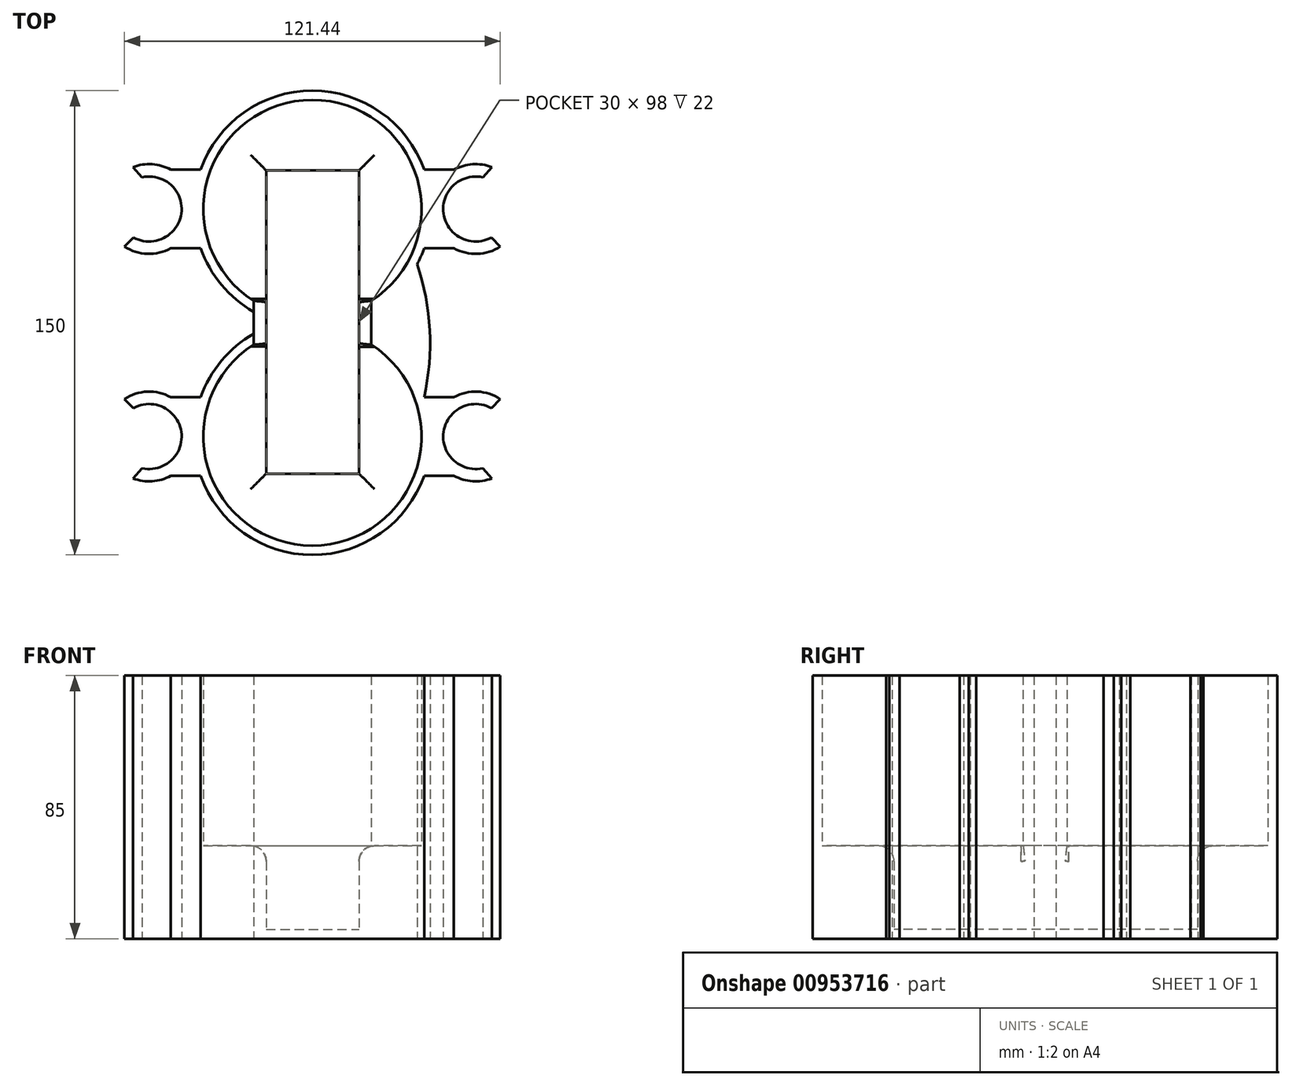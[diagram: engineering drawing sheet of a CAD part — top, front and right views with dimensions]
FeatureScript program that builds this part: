
annotation { "Feature Type Name" : "Feature", "Feature Type Description" : "" }
export const myFeature = defineFeature(function(context is Context, id is Id, definition is map)
    precondition{}
    {
        {
            var Q0;
            Q0=qCreatedBy(makeId("Top.planeOp"),FACE);
            var sketch = newSketch(context, id + "F0", { "sketchPlane" : qUnion([Q0])});
            skCircle(sketch, "E0", {"center": v(0, 36.75) * mm, "radius": 35.25 * mm});
            skCircle(sketch, "E1.0", {"center": v(0, 36.75) * mm, "radius": 38.25 * mm});
            skCircle(sketch, "E2", {"center": v(0, -36.75) * mm, "radius": 35.25 * mm});
            skCircle(sketch, "E3.0", {"center": v(0, -36.75) * mm, "radius": 38.25 * mm});
            skLineSegment(sketch, "E4.bottom", {"start": v(-14.94, 49.23) * mm, "end": v(15.06, 49.23) * mm});
            skLineSegment(sketch, "E4.top", {"start": v(-14.94, -48.77) * mm, "end": v(15.06, -48.77) * mm});
            skLineSegment(sketch, "E4.left", {"start": v(-14.94, 49.23) * mm, "end": v(-14.94, -48.77) * mm});
            skLineSegment(sketch, "E4.right", {"start": v(15.06, 49.23) * mm, "end": v(15.06, -48.77) * mm});
            skLineSegment(sketch, "E5", {"start": v(19, 7.06) * mm, "end": v(19, -7.06) * mm});
            skLineSegment(sketch, "E6.MirrorCS", {"start": v(-19, 7.06) * mm, "end": v(-19, -7.06) * mm});
            skArc(sketch, "E7", {"start": v(36.08, -24.06) * mm, "mid": v(37.91, -2.41) * mm, "end": v(33.85, 18.94) * mm});
            skArc(sketch, "E8.MirrorCS", {"start": v(-36.08, -24.06) * mm, "mid": v(-37.91, -2.41) * mm, "end": v(-33.85, 18.94) * mm});
            skCircle(sketch, "E9", {"center": v(-52.75, 36.75) * mm, "radius": 10.5 * mm});
            skCircle(sketch, "E10.0", {"center": v(-52.75, 36.75) * mm, "radius": 14.5 * mm});
            skLineSegment(sketch, "E11", {"start": v(-57.8, 27.55) * mm, "end": v(-60.72, 24.64) * mm});
            skLineSegment(sketch, "E12", {"start": v(-55.03, 47) * mm, "end": v(-57.98, 50.27) * mm});
            skCircle(sketch, "E13.MirrorC", {"center": v(52.75, 36.75) * mm, "radius": 14.5 * mm});
            skCircle(sketch, "E14.MirrorC", {"center": v(52.75, 36.75) * mm, "radius": 10.5 * mm});
            skLineSegment(sketch, "E15.MirrorCS", {"start": v(55.03, 47) * mm, "end": v(57.98, 50.27) * mm});
            skLineSegment(sketch, "E16.MirrorCS", {"start": v(57.8, 27.55) * mm, "end": v(60.72, 24.64) * mm});
            skLineSegment(sketch, "E17.MirrorCS", {"start": v(-57.8, -27.55) * mm, "end": v(-60.72, -24.64) * mm});
            skCircle(sketch, "E18.MirrorC", {"center": v(-52.75, -36.75) * mm, "radius": 14.5 * mm});
            skCircle(sketch, "E19.MirrorC", {"center": v(-52.75, -36.75) * mm, "radius": 10.5 * mm});
            skLineSegment(sketch, "E20.MirrorCS", {"start": v(-55.03, -47) * mm, "end": v(-57.98, -50.27) * mm});
            skCircle(sketch, "E21.MirrorC", {"center": v(52.75, -36.75) * mm, "radius": 10.5 * mm});
            skCircle(sketch, "E22.MirrorC", {"center": v(52.75, -36.75) * mm, "radius": 14.5 * mm});
            skLineSegment(sketch, "E23.MirrorCS", {"start": v(55.03, -47) * mm, "end": v(57.98, -50.27) * mm});
            skLineSegment(sketch, "E24.MirrorCS", {"start": v(57.8, -27.55) * mm, "end": v(60.72, -24.64) * mm});
            skLineSegment(sketch, "E25", {"start": v(-45.73, -24.06) * mm, "end": v(-36.08, -24.06) * mm});
            skLineSegment(sketch, "E26", {"start": v(-45.73, -49.44) * mm, "end": v(-36.08, -49.44) * mm});
            skLineSegment(sketch, "E27.MirrorCS", {"start": v(45.73, -24.06) * mm, "end": v(36.08, -24.06) * mm});
            skLineSegment(sketch, "E28.MirrorCS", {"start": v(45.73, -49.44) * mm, "end": v(36.08, -49.44) * mm});
            skLineSegment(sketch, "E29.MirrorCS", {"start": v(-45.73, 24.06) * mm, "end": v(-36.08, 24.06) * mm});
            skLineSegment(sketch, "E30.MirrorCS", {"start": v(-45.73, 49.44) * mm, "end": v(-36.08, 49.44) * mm});
            skLineSegment(sketch, "E31.MirrorCS", {"start": v(45.73, 49.44) * mm, "end": v(36.08, 49.44) * mm});
            skLineSegment(sketch, "E32.MirrorCS", {"start": v(45.73, 24.06) * mm, "end": v(36.08, 24.06) * mm});
            skSolve(sketch);
        }
        {
            var Q0;
            {var subQ9=sQuery(id+"F0.wireOp",EDGE,"E5");var subQ10=sQuery(id+"F0.wireOp",EDGE,"E0");var subQ11=makeQuery(id+"F0.imprint","INTERSECT",VERTEX,{"derivedFrom":[subQ10,subQ9]});Q0=makeQuery(id+"F0.imprint","IMPRINT",FACE,{"disambiguationData":[TD([[makeQuery(id+"F0.imprint","IMPRINT",EDGE,{"disambiguationData":[TD([[subQ11,-1.0]])],"derivedFrom":subQ10}),-1.0]])]});}
            var Q1;
            {var subQ0=sQuery(id+"F0.wireOp",EDGE,"E8.MirrorCS");Q1=makeQuery(id+"F0.imprint","IMPRINT",FACE,{"disambiguationData":[TD([[makeQuery(id+"F0.imprint","IMPRINT",EDGE,{"derivedFrom":subQ0}),-1.0]])]});}
            var Q2;
            {var subQ0=sQuery(id+"F0.wireOp",EDGE,"E7");Q2=makeQuery(id+"F0.imprint","IMPRINT",FACE,{"disambiguationData":[TD([[makeQuery(id+"F0.imprint","IMPRINT",EDGE,{"derivedFrom":subQ0}),1.0]])]});}
            var Q3;
            {var subQ0=sQuery(id+"F0.wireOp",EDGE,"E5");var subQ1=sQuery(id+"F0.wireOp",EDGE,"E2");var subQ2=makeQuery(id+"F0.imprint","INTERSECT",VERTEX,{"derivedFrom":[subQ1,subQ0]});Q3=makeQuery(id+"F0.imprint","IMPRINT",FACE,{"disambiguationData":[TD([[makeQuery(id+"F0.imprint","IMPRINT",EDGE,{"disambiguationData":[TD([[subQ2,1.0]])],"derivedFrom":subQ1}),-1.0]])]});}
            extrude(context, id + "F1", {"entities" : qUnion([Q0, Q1, Q2, Q3]), "depth" : 85 * mm, "offsetDistance" : 25 * mm});
        }
        {
            var Q0;
            {var subQ0=sQuery(id+"F0.wireOp",EDGE,"E6.MirrorCS");var subQ1=sQuery(id+"F0.wireOp",EDGE,"E1.0");var subQ2=makeQuery(id+"F0.imprint","INTERSECT",VERTEX,{"derivedFrom":[subQ1,subQ0]});Q0=makeQuery(id+"F0.imprint","IMPRINT",FACE,{"disambiguationData":[TD([[makeQuery(id+"F0.imprint","IMPRINT",EDGE,{"disambiguationData":[TD([[subQ2,-1.0]])],"derivedFrom":subQ1}),-1.0]])]});}
            var Q1;
            {var subQ0=sQuery(id+"F0.wireOp",EDGE,"E6.MirrorCS");var subQ1=sQuery(id+"F0.wireOp",EDGE,"E0");var subQ2=makeQuery(id+"F0.imprint","INTERSECT",VERTEX,{"derivedFrom":[subQ1,subQ0]});Q1=makeQuery(id+"F0.imprint","IMPRINT",FACE,{"disambiguationData":[TD([[makeQuery(id+"F0.imprint","IMPRINT",EDGE,{"disambiguationData":[TD([[subQ2,-1.0]])],"derivedFrom":subQ1}),-1.0]])]});}
            var Q2;
            {var subQ0=sQuery(id+"F0.wireOp",EDGE,"E6.MirrorCS");var subQ1=sQuery(id+"F0.wireOp",EDGE,"E2");var subQ2=makeQuery(id+"F0.imprint","INTERSECT",VERTEX,{"derivedFrom":[subQ1,subQ0]});Q2=makeQuery(id+"F0.imprint","IMPRINT",FACE,{"disambiguationData":[TD([[makeQuery(id+"F0.imprint","IMPRINT",EDGE,{"disambiguationData":[TD([[subQ2,1.0]])],"derivedFrom":subQ1}),-1.0]])]});}
            var Q3;
            {var subQ0=sQuery(id+"F0.wireOp",EDGE,"E4.right");var subQ1=sQuery(id+"F0.wireOp",EDGE,"E1.0");var subQ2=makeQuery(id+"F0.imprint","INTERSECT",VERTEX,{"derivedFrom":[subQ1,subQ0]});Q3=makeQuery(id+"F0.imprint","IMPRINT",FACE,{"disambiguationData":[TD([[makeQuery(id+"F0.imprint","IMPRINT",EDGE,{"disambiguationData":[TD([[subQ2,-1.0]])],"derivedFrom":subQ1}),-1.0]])]});}
            var Q4;
            {var subQ0=sQuery(id+"F0.wireOp",EDGE,"E5");var subQ1=sQuery(id+"F0.wireOp",EDGE,"E2");var subQ2=makeQuery(id+"F0.imprint","INTERSECT",VERTEX,{"derivedFrom":[subQ1,subQ0]});Q4=makeQuery(id+"F0.imprint","IMPRINT",FACE,{"disambiguationData":[TD([[makeQuery(id+"F0.imprint","IMPRINT",EDGE,{"disambiguationData":[TD([[subQ2,-1.0]])],"derivedFrom":subQ1}),-1.0]])]});}
            var Q5;
            {var subQ0=sQuery(id+"F0.wireOp",EDGE,"E5");var subQ1=sQuery(id+"F0.wireOp",EDGE,"E0");var subQ2=makeQuery(id+"F0.imprint","INTERSECT",VERTEX,{"derivedFrom":[subQ1,subQ0]});Q5=makeQuery(id+"F0.imprint","IMPRINT",FACE,{"disambiguationData":[TD([[makeQuery(id+"F0.imprint","IMPRINT",EDGE,{"disambiguationData":[TD([[subQ2,1.0]])],"derivedFrom":subQ1}),-1.0]])]});}
            var Q6;
            {var subQ0=sQuery(id+"F0.wireOp",EDGE,"E4.top");Q6=makeQuery(id+"F0.imprint","IMPRINT",FACE,{"disambiguationData":[TD([[makeQuery(id+"F0.imprint","IMPRINT",EDGE,{"derivedFrom":subQ0}),-1.0]])]});}
            var Q7;
            {var subQ3=sQuery(id+"F0.wireOp",EDGE,"E4.bottom");Q7=makeQuery(id+"F0.imprint","IMPRINT",FACE,{"disambiguationData":[TD([[makeQuery(id+"F0.imprint","IMPRINT",EDGE,{"derivedFrom":subQ3}),1.0]])]});}
            extrude(context, id + "F2", {"entities" : qUnion([Q0, Q1, Q2, Q3, Q4, Q5, Q6, Q7]), "operationType" : NewBodyOperationType.ADD, "depth" : 30 * mm, "offsetDistance" : 25 * mm});
        }
        {
            var Q0;
            {var subQ1=sQuery(id+"F0.wireOp",EDGE,"E4.bottom");Q0=makeQuery(id+"F0.imprint","IMPRINT",FACE,{"disambiguationData":[TD([[makeQuery(id+"F0.imprint","IMPRINT",EDGE,{"derivedFrom":subQ1}),-1.0]])]});}
            var Q1;
            {var subQ0=sQuery(id+"F0.wireOp",EDGE,"E3.0");var subQ1=sQuery(id+"F0.wireOp",EDGE,"E1.0");var subQ2=makeQuery(id+"F0.imprint","INTERSECT",VERTEX,{"disambiguationData":[OD(0.0)],"derivedFrom":[subQ1,subQ0]});Q1=makeQuery(id+"F0.imprint","IMPRINT",FACE,{"disambiguationData":[TD([[makeQuery(id+"F0.imprint","IMPRINT",EDGE,{"disambiguationData":[TD([[subQ2,-1.0]])],"derivedFrom":subQ1}),1.0]])]});}
            var Q2;
            {var subQ0=sQuery(id+"F0.wireOp",EDGE,"E4.left");var subQ1=sQuery(id+"F0.wireOp",EDGE,"E0");var subQ2=makeQuery(id+"F0.imprint","INTERSECT",VERTEX,{"derivedFrom":[subQ1,subQ0]});Q2=makeQuery(id+"F0.imprint","IMPRINT",FACE,{"disambiguationData":[TD([[makeQuery(id+"F0.imprint","IMPRINT",EDGE,{"disambiguationData":[TD([[subQ2,-1.0]])],"derivedFrom":subQ1}),-1.0]])]});}
            var Q3;
            {var subQ0=sQuery(id+"F0.wireOp",EDGE,"E3.0");var subQ1=sQuery(id+"F0.wireOp",EDGE,"E0");var subQ2=makeQuery(id+"F0.imprint","INTERSECT",VERTEX,{"derivedFrom":[subQ1,subQ0]});Q3=makeQuery(id+"F0.imprint","IMPRINT",FACE,{"disambiguationData":[TD([[makeQuery(id+"F0.imprint","IMPRINT",EDGE,{"disambiguationData":[TD([[subQ2,-1.0]])],"derivedFrom":subQ1}),-1.0]])]});}
            var Q4;
            {var subQ0=sQuery(id+"F0.wireOp",EDGE,"E3.0");var subQ1=sQuery(id+"F0.wireOp",EDGE,"E1.0");var subQ2=makeQuery(id+"F0.imprint","INTERSECT",VERTEX,{"disambiguationData":[OD(1.0)],"derivedFrom":[subQ1,subQ0]});Q4=makeQuery(id+"F0.imprint","IMPRINT",FACE,{"disambiguationData":[TD([[makeQuery(id+"F0.imprint","IMPRINT",EDGE,{"disambiguationData":[TD([[subQ2,-1.0]])],"derivedFrom":subQ1}),-1.0]])]});}
            var Q5;
            {var subQ0=sQuery(id+"F0.wireOp",EDGE,"E2");var subQ1=sQuery(id+"F0.wireOp",EDGE,"E1.0");var subQ2=makeQuery(id+"F0.imprint","INTERSECT",VERTEX,{"derivedFrom":[subQ1,subQ0]});Q5=makeQuery(id+"F0.imprint","IMPRINT",FACE,{"disambiguationData":[TD([[makeQuery(id+"F0.imprint","IMPRINT",EDGE,{"disambiguationData":[TD([[subQ2,-1.0]])],"derivedFrom":subQ1}),-1.0]])]});}
            var Q6;
            {var subQ0=sQuery(id+"F0.wireOp",EDGE,"E4.left");var subQ1=sQuery(id+"F0.wireOp",EDGE,"E1.0");var subQ2=makeQuery(id+"F0.imprint","INTERSECT",VERTEX,{"derivedFrom":[subQ1,subQ0]});Q6=makeQuery(id+"F0.imprint","IMPRINT",FACE,{"disambiguationData":[TD([[makeQuery(id+"F0.imprint","IMPRINT",EDGE,{"disambiguationData":[TD([[subQ2,-1.0]])],"derivedFrom":subQ1}),-1.0]])]});}
            var Q7;
            {var subQ0=sQuery(id+"F0.wireOp",EDGE,"E3.0");var subQ1=sQuery(id+"F0.wireOp",EDGE,"E1.0");var subQ2=makeQuery(id+"F0.imprint","INTERSECT",VERTEX,{"disambiguationData":[OD(0.0)],"derivedFrom":[subQ1,subQ0]});Q7=makeQuery(id+"F0.imprint","IMPRINT",FACE,{"disambiguationData":[TD([[makeQuery(id+"F0.imprint","IMPRINT",EDGE,{"disambiguationData":[TD([[subQ2,-1.0]])],"derivedFrom":subQ1}),-1.0]])]});}
            var Q8;
            {var subQ1=sQuery(id+"F0.wireOp",EDGE,"E4.top");Q8=makeQuery(id+"F0.imprint","IMPRINT",FACE,{"disambiguationData":[TD([[makeQuery(id+"F0.imprint","IMPRINT",EDGE,{"derivedFrom":subQ1}),1.0]])]});}
            extrude(context, id + "F3", {"entities" : qUnion([Q0, Q1, Q2, Q3, Q4, Q5, Q6, Q7, Q8]), "operationType" : NewBodyOperationType.ADD, "depth" : 3 * mm, "offsetDistance" : 25 * mm});
        }
        {
            var Q0;
            {var subQ0=sQuery(id+"F0.wireOp",EDGE,"E31.MirrorCS");Q0=makeQuery(id+"F0.imprint","IMPRINT",FACE,{"disambiguationData":[TD([[makeQuery(id+"F0.imprint","IMPRINT",EDGE,{"derivedFrom":subQ0}),1.0]])]});}
            var Q1;
            {var subQ0=sQuery(id+"F0.wireOp",EDGE,"E32.MirrorCS");Q1=makeQuery(id+"F0.imprint","IMPRINT",FACE,{"disambiguationData":[TD([[makeQuery(id+"F0.imprint","IMPRINT",EDGE,{"derivedFrom":subQ0}),-1.0]])]});}
            var Q2;
            {var subQ6=sQuery(id+"F0.wireOp",EDGE,"E15.MirrorCS");Q2=makeQuery(id+"F0.imprint","IMPRINT",FACE,{"disambiguationData":[TD([[makeQuery(id+"F0.imprint","IMPRINT",EDGE,{"derivedFrom":subQ6}),1.0]])]});}
            extrude(context, id + "F4", {"entities" : qUnion([Q0, Q1, Q2]), "operationType" : NewBodyOperationType.ADD, "depth" : 85 * mm, "offsetDistance" : 25 * mm});
        }
        {
            var Q0;
            {var subQ0=sQuery(id+"F0.wireOp",EDGE,"E28.MirrorCS");Q0=makeQuery(id+"F0.imprint","IMPRINT",FACE,{"disambiguationData":[TD([[makeQuery(id+"F0.imprint","IMPRINT",EDGE,{"derivedFrom":subQ0}),-1.0]])]});}
            var Q1;
            {var subQ0=sQuery(id+"F0.wireOp",EDGE,"E27.MirrorCS");Q1=makeQuery(id+"F0.imprint","IMPRINT",FACE,{"disambiguationData":[TD([[makeQuery(id+"F0.imprint","IMPRINT",EDGE,{"derivedFrom":subQ0}),1.0]])]});}
            var Q2;
            {var subQ5=sQuery(id+"F0.wireOp",EDGE,"E23.MirrorCS");Q2=makeQuery(id+"F0.imprint","IMPRINT",FACE,{"disambiguationData":[TD([[makeQuery(id+"F0.imprint","IMPRINT",EDGE,{"derivedFrom":subQ5}),-1.0]])]});}
            var Q3;
            {var subQ3=sQuery(id+"F0.wireOp",EDGE,"E11");Q3=makeQuery(id+"F0.imprint","IMPRINT",FACE,{"disambiguationData":[TD([[makeQuery(id+"F0.imprint","IMPRINT",EDGE,{"derivedFrom":subQ3}),1.0]])]});}
            var Q4;
            {var subQ0=sQuery(id+"F0.wireOp",EDGE,"E29.MirrorCS");Q4=makeQuery(id+"F0.imprint","IMPRINT",FACE,{"disambiguationData":[TD([[makeQuery(id+"F0.imprint","IMPRINT",EDGE,{"derivedFrom":subQ0}),1.0]])]});}
            var Q5;
            {var subQ0=sQuery(id+"F0.wireOp",EDGE,"E30.MirrorCS");Q5=makeQuery(id+"F0.imprint","IMPRINT",FACE,{"disambiguationData":[TD([[makeQuery(id+"F0.imprint","IMPRINT",EDGE,{"derivedFrom":subQ0}),-1.0]])]});}
            var Q6;
            {var subQ3=sQuery(id+"F0.wireOp",EDGE,"E17.MirrorCS");Q6=makeQuery(id+"F0.imprint","IMPRINT",FACE,{"disambiguationData":[TD([[makeQuery(id+"F0.imprint","IMPRINT",EDGE,{"derivedFrom":subQ3}),-1.0]])]});}
            var Q7;
            {var subQ0=sQuery(id+"F0.wireOp",EDGE,"E25");Q7=makeQuery(id+"F0.imprint","IMPRINT",FACE,{"disambiguationData":[TD([[makeQuery(id+"F0.imprint","IMPRINT",EDGE,{"derivedFrom":subQ0}),-1.0]])]});}
            var Q8;
            {var subQ0=sQuery(id+"F0.wireOp",EDGE,"E26");Q8=makeQuery(id+"F0.imprint","IMPRINT",FACE,{"disambiguationData":[TD([[makeQuery(id+"F0.imprint","IMPRINT",EDGE,{"derivedFrom":subQ0}),1.0]])]});}
            extrude(context, id + "F5", {"entities" : qUnion([Q0, Q1, Q2, Q3, Q4, Q5, Q6, Q7, Q8]), "operationType" : NewBodyOperationType.ADD, "depth" : 85 * mm, "offsetDistance" : 25 * mm});
        }
        {
            var Q0;
            Q0=makeQuery(id+"F2.opExtrude","CAP_EDGE",EDGE,{"disambiguationData":[OSD([sQuery(id+"F0.wireOp",EDGE,"E4.bottom")])],"isStart":false});
            var Q1;
            Q1=makeQuery(id+"F2.opExtrude","CAP_EDGE",EDGE,{"disambiguationData":[OSD([sQuery(id+"F0.wireOp",EDGE,"E4.right")])],"isStart":false});
            var Q2;
            Q2=makeQuery(id+"F2.opExtrude","CAP_EDGE",EDGE,{"disambiguationData":[OSD([sQuery(id+"F0.wireOp",EDGE,"E4.top")])],"isStart":false});
            var Q3;
            Q3=makeQuery(id+"F2.opExtrude","CAP_EDGE",EDGE,{"disambiguationData":[OSD([sQuery(id+"F0.wireOp",EDGE,"E4.left")])],"isStart":false});
            fillet(context, id + "F6", {"entities" : qUnion([Q0, Q1, Q2, Q3]), "radius" : 5 * mm, "tangentPropagation" : true, "allowEdgeOverflow" : false});
        }
    });
